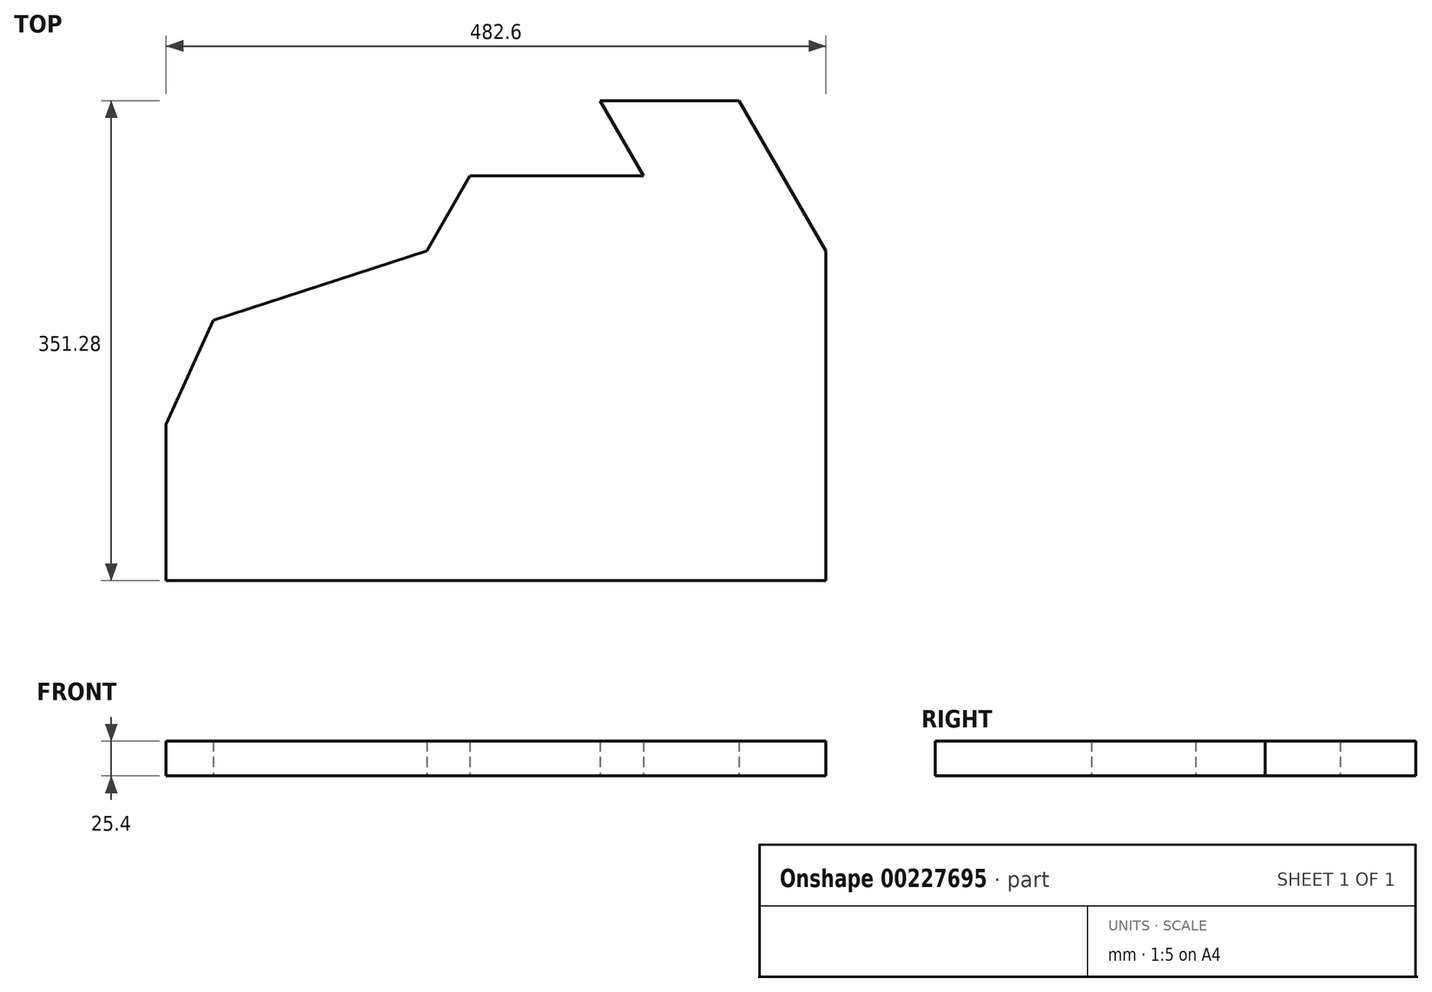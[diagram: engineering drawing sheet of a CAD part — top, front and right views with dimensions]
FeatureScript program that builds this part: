
annotation { "Feature Type Name" : "Feature", "Feature Type Description" : "" }
export const myFeature = defineFeature(function(context is Context, id is Id, definition is map)
    precondition{}
    {
        {
            var Q0;
            Q0=qCreatedBy(makeId("Top.planeOp"),FACE);
            var sketch = newSketch(context, id + "F0", { "sketchPlane" : qUnion([Q0])});
            skLineSegment(sketch, "E0", {"start": v(-281.95, -140.78) * mm, "end": v(200.65, -140.78) * mm});
            skLineSegment(sketch, "E1", {"start": v(200.65, -140.78) * mm, "end": v(200.65, 100.52) * mm});
            skLineSegment(sketch, "E2", {"start": v(200.65, 100.52) * mm, "end": v(137.15, 210.5) * mm});
            skLineSegment(sketch, "E3", {"start": v(137.15, 210.5) * mm, "end": v(35.55, 210.5) * mm});
            skLineSegment(sketch, "E4", {"start": v(35.55, 210.5) * mm, "end": v(67.34, 155.54) * mm});
            skLineSegment(sketch, "E5", {"start": v(67.34, 155.54) * mm, "end": v(-59.66, 155.54) * mm});
            skLineSegment(sketch, "E6", {"start": v(-59.66, 155.54) * mm, "end": v(-91.36, 100.52) * mm});
            skLineSegment(sketch, "E7", {"start": v(-91.36, 100.52) * mm, "end": v(-247.59, 49.72) * mm});
            skLineSegment(sketch, "E8", {"start": v(-281.95, -140.78) * mm, "end": v(-281.95, -26.48) * mm});
            skLineSegment(sketch, "E9", {"start": v(-247.59, 49.72) * mm, "end": v(-281.95, -26.48) * mm});
            skLineSegment(sketch, "E10", {"start": v(200.65, 100.52) * mm, "end": v(200.65, 210.68) * mm});
            skSolve(sketch);
        }
        {
            var Q0;
            Q0=makeQuery(id+"F0.imprint","IMPRINT",FACE,{"disambiguationData":[TD([[makeQuery(id+"F0.imprint","IMPRINT",EDGE,{"derivedFrom":sQuery(id+"F0.wireOp",EDGE,"E0")}),1.0]])]});
            extrude(context, id + "F1", {"entities" : qUnion([Q0]), "depth" : 25.4 * mm});
        }
    });
